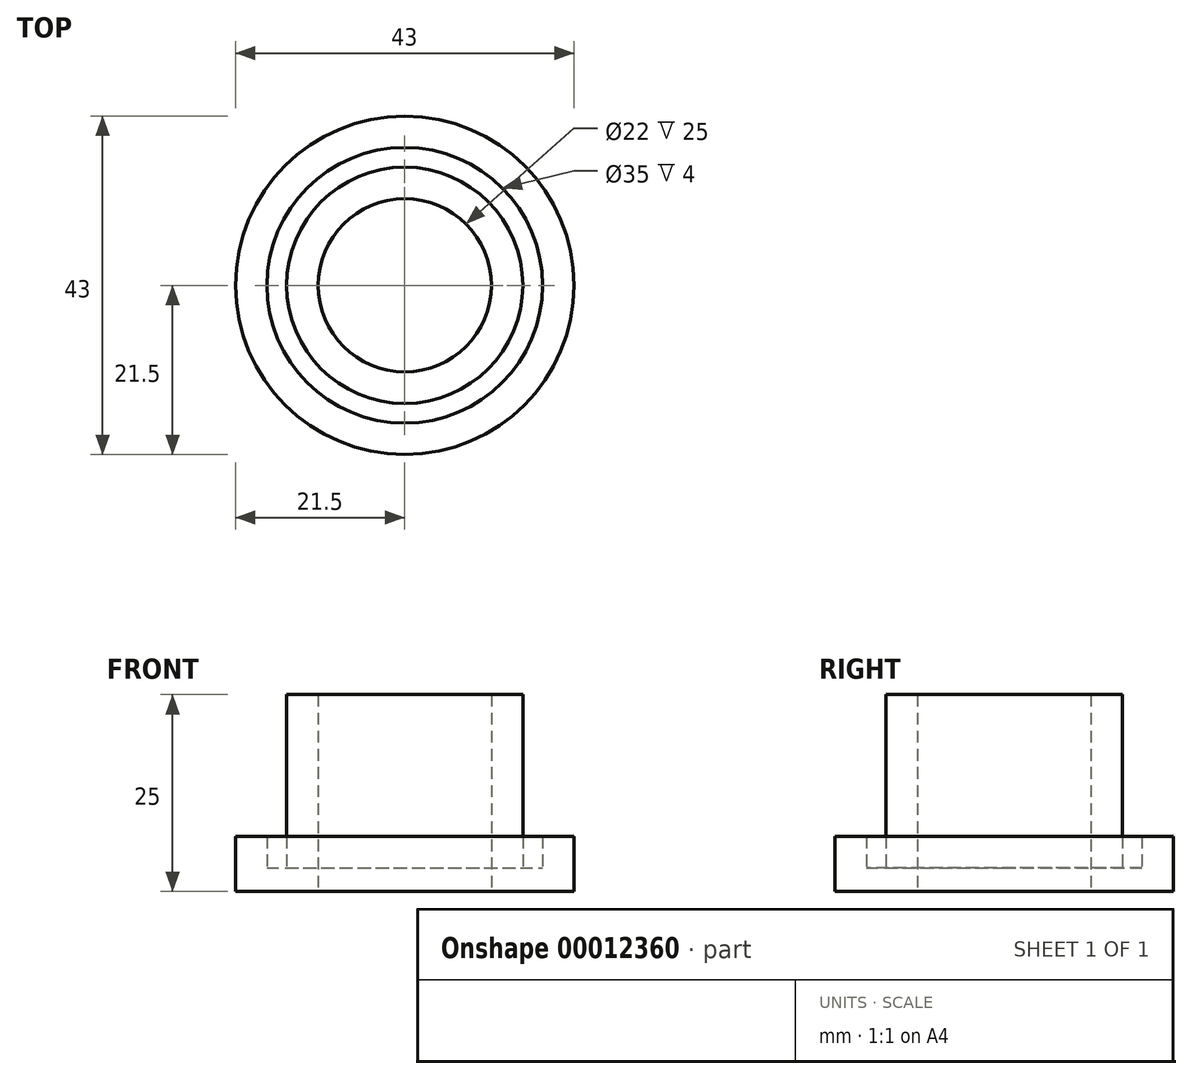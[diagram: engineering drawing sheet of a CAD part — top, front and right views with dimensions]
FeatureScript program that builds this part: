
annotation { "Feature Type Name" : "Feature", "Feature Type Description" : "" }
export const myFeature = defineFeature(function(context is Context, id is Id, definition is map)
    precondition{}
    {
        {
            var Q0;
            Q0=qCreatedBy(makeId("Front.planeOp"),FACE);
            var sketch = newSketch(context, id + "F0", { "sketchPlane" : qUnion([Q0])});
            skLineSegment(sketch, "E0", {"start": v(0, 0) * mm, "end": v(21.5, 0) * mm});
            skLineSegment(sketch, "E1", {"start": v(21.5, 0) * mm, "end": v(21.5, 7) * mm});
            skLineSegment(sketch, "E2", {"start": v(21.5, 7) * mm, "end": v(17.5, 7) * mm});
            skLineSegment(sketch, "E3", {"start": v(17.5, 7) * mm, "end": v(17.5, 3) * mm});
            skLineSegment(sketch, "E4", {"start": v(17.5, 3) * mm, "end": v(15, 3) * mm});
            skLineSegment(sketch, "E5", {"start": v(15, 3) * mm, "end": v(15, 25) * mm});
            skLineSegment(sketch, "E6", {"start": v(15, 25) * mm, "end": v(11, 25) * mm});
            skLineSegment(sketch, "E7", {"start": v(11, 25) * mm, "end": v(11, 3) * mm});
            skLineSegment(sketch, "E8", {"start": v(11, 3) * mm, "end": v(0, 3) * mm});
            skLineSegment(sketch, "E9", {"start": v(0, 0) * mm, "end": v(0, 32.53) * mm, "construction": true});
            skLineSegment(sketch, "E10.0.MirrorCS", {"start": v(-11, 3) * mm, "end": v(0, 3) * mm});
            skLineSegment(sketch, "E11.0.MirrorCS", {"start": v(-11, 25) * mm, "end": v(-11, 3) * mm});
            skLineSegment(sketch, "E12.0.MirrorCS", {"start": v(-15, 3) * mm, "end": v(-15, 25) * mm});
            skLineSegment(sketch, "E13.0.MirrorCS", {"start": v(-15, 25) * mm, "end": v(-11, 25) * mm});
            skLineSegment(sketch, "E14.0.MirrorCS", {"start": v(-17.5, 3) * mm, "end": v(-15, 3) * mm});
            skLineSegment(sketch, "E15.0.MirrorCS", {"start": v(-17.5, 7) * mm, "end": v(-17.5, 3) * mm});
            skLineSegment(sketch, "E16.0.MirrorCS", {"start": v(-21.5, 7) * mm, "end": v(-17.5, 7) * mm});
            skLineSegment(sketch, "E17.0.MirrorCS", {"start": v(-21.5, 0) * mm, "end": v(-21.5, 7) * mm});
            skLineSegment(sketch, "E18.0.MirrorCS", {"start": v(0, 0) * mm, "end": v(-21.5, 0) * mm});
            skLineSegment(sketch, "E19", {"start": v(0, 3) * mm, "end": v(0, 0) * mm});
            skSolve(sketch);
        }
        {
            var Q0;
            Q0=makeQuery(id+"F0.imprint","IMPRINT",FACE,{"disambiguationData":[TD([[makeQuery(id+"F0.imprint","IMPRINT",EDGE,{"derivedFrom":sQuery(id+"F0.wireOp",EDGE,"E10.0.MirrorCS")}),-1.0]])]});
            var Q1;
            Q1=sQuery(id+"F0.wireOp",EDGE,"E9");
            revolve(context, id + "F1", {"entities" : qUnion([Q0]), "axis" : qUnion([Q1]), "revolveType" : RevolveType.FULL});
        }
        {
            var Q0;
            Q0=makeQuery(id+"F1.opRevolve","SWEPT_FACE",FACE,{"disambiguationData":[OSD([sQuery(id+"F0.wireOp",EDGE,"E10.0.MirrorCS")])]});
            var sketch = newSketch(context, id + "F2", { "sketchPlane" : qUnion([Q0])});
            skSolve(sketch);
        }
        {
            var Q0;
            Q0 = qSketchRegion(id + "F2", true);
            var Q1;
            Q1=makeQuery(id+"F2.imprint","IMPRINT",FACE,{"disambiguationData":[TD([[makeQuery(id+"F2.imprint","IMPRINT",EDGE,{"derivedFrom":makeQuery(id+"F1.opRevolve","SWEPT_EDGE",EDGE,{"disambiguationData":[OSD([sQuery(id+"F0.wireOp",EDGE,"E10.0.MirrorCS"),sQuery(id+"F0.wireOp",EDGE,"E11.0.MirrorCS")])]})}),-1.0]])]});
            extrude(context, id + "F3", {"entities" : qUnion([Q0, Q1]), "operationType" : NewBodyOperationType.REMOVE, "endBound" : BoundingType.THROUGH_ALL, "oppositeDirection" : true, "depth" : 25 * mm});
        }
    });
